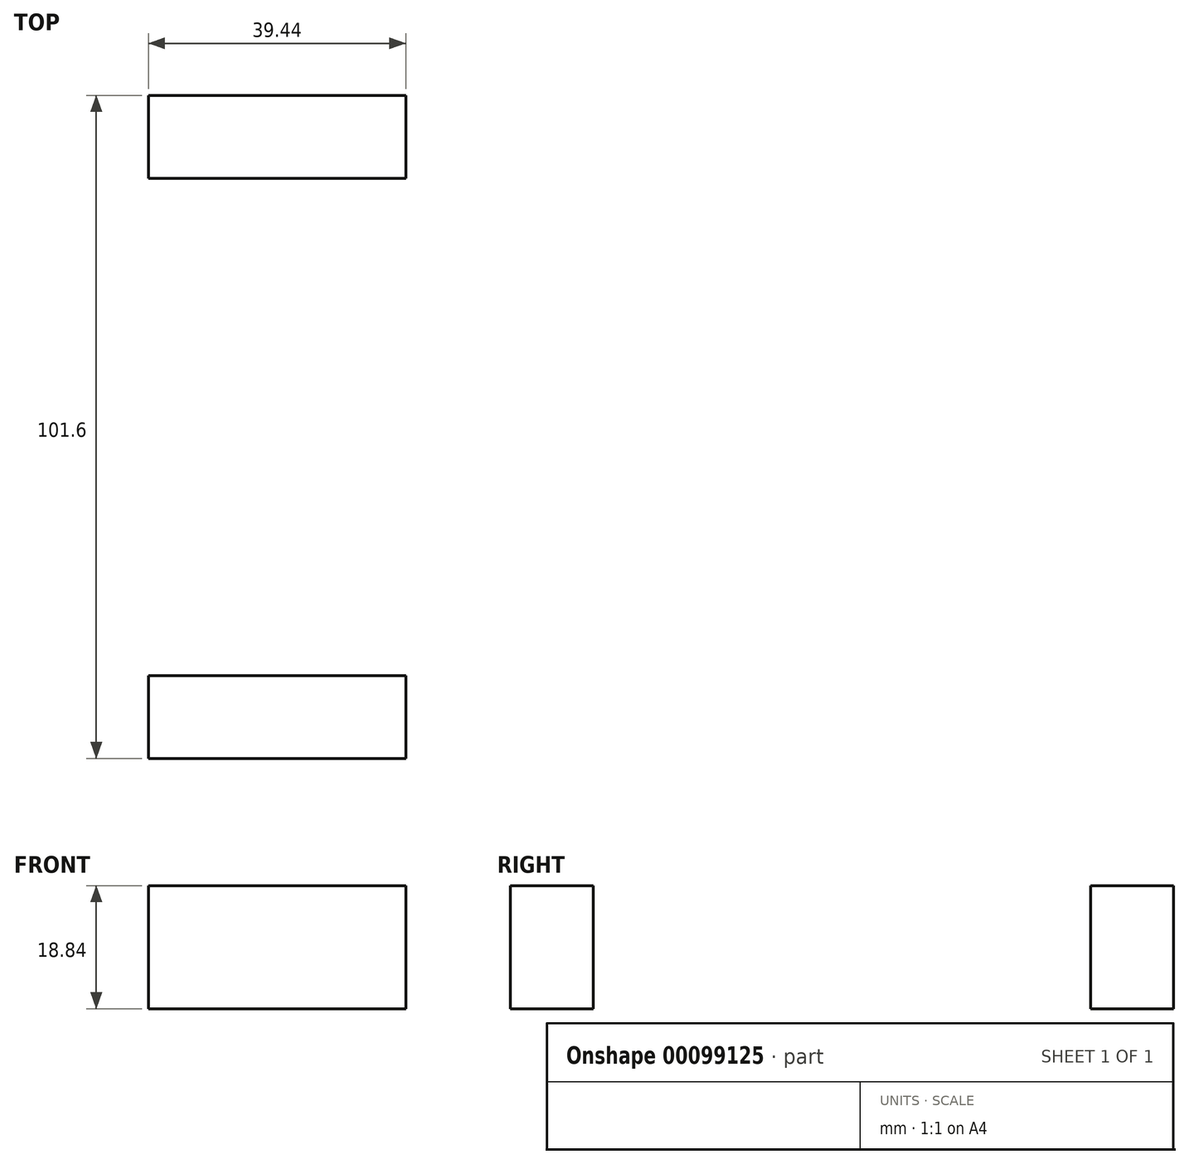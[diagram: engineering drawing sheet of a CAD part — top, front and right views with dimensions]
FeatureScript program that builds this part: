
annotation { "Feature Type Name" : "Feature", "Feature Type Description" : "" }
export const myFeature = defineFeature(function(context is Context, id is Id, definition is map)
    precondition{}
    {
        {
            var Q0;
            Q0=qCreatedBy(makeId("Front.planeOp"),FACE);
            var sketch = newSketch(context, id + "F0", { "sketchPlane" : qUnion([Q0])});
            skLineSegment(sketch, "E0.bottom", {"start": v(19.72, -9.42) * mm, "end": v(-19.72, -9.42) * mm});
            skLineSegment(sketch, "E0.top", {"start": v(19.72, 9.42) * mm, "end": v(-19.72, 9.42) * mm});
            skLineSegment(sketch, "E0.left", {"start": v(19.72, -9.42) * mm, "end": v(19.72, 9.42) * mm});
            skLineSegment(sketch, "E0.right", {"start": v(-19.72, -9.42) * mm, "end": v(-19.72, 9.42) * mm});
            skPoint(sketch, "E0.middle", {"position": v(0, 0) * mm});
            skLineSegment(sketch, "E1.bottom", {"start": v(62.56, 20.27) * mm, "end": v(34.5, 20.27) * mm});
            skLineSegment(sketch, "E1.top", {"start": v(62.56, 37.89) * mm, "end": v(34.5, 37.89) * mm});
            skLineSegment(sketch, "E1.left", {"start": v(62.56, 20.27) * mm, "end": v(62.56, 37.89) * mm});
            skLineSegment(sketch, "E1.right", {"start": v(34.5, 20.27) * mm, "end": v(34.5, 37.89) * mm});
            skPoint(sketch, "E1.middle", {"position": v(48.53, 29.08) * mm});
            skLineSegment(sketch, "E2", {"start": v(19.72, 9.42) * mm, "end": v(19.72, 16.44) * mm});
            skArc(sketch, "E3", {"start": v(19.72, 16.44) * mm, "mid": v(21.34, 20.37) * mm, "end": v(25.27, 22) * mm});
            skLineSegment(sketch, "E4", {"start": v(25.27, 22) * mm, "end": v(47.52, 22) * mm});
            skLineSegment(sketch, "E5.0", {"start": v(25.27, 33.09) * mm, "end": v(47.52, 33.09) * mm});
            skArc(sketch, "E5.1", {"start": v(8.62, 16.44) * mm, "mid": v(13.5, 28.21) * mm, "end": v(25.27, 33.09) * mm});
            skLineSegment(sketch, "E5.2", {"start": v(8.62, 9.1) * mm, "end": v(8.62, 16.44) * mm});
            skFitSpline(sketch, "E6", {"points": [v(-19.72, 9.42) * mm, v(25.27, 33.09) * mm], "startDerivative": vector(-0.22, 63.1) * mm, "endDerivative": vector(75.8, 0) * mm});
            skSolve(sketch);
        }
        {
            var Q0;
            Q0=makeQuery(id+"F0.imprint","IMPRINT",FACE,{"disambiguationData":[TD([[makeQuery(id+"F0.imprint","IMPRINT",EDGE,{"derivedFrom":sQuery(id+"F0.wireOp",EDGE,"E0.bottom")}),-1.0]])]});
            extrude(context, id + "F1", {"entities" : qUnion([Q0]), "endBound" : BoundingType.SYMMETRIC, "depth" : 101.6 * mm});
        }
        {
            var Q0;
            Q0=makeQuery(id+"F0.imprint","IMPRINT",FACE,{"disambiguationData":[TD([[makeQuery(id+"F0.imprint","IMPRINT",EDGE,{"derivedFrom":sQuery(id+"F0.wireOp",EDGE,"E0.bottom")}),-1.0]])]});
            var Q1;
            {var subQ5=sQuery(id+"F0.wireOp",EDGE,"E2");Q1=makeQuery(id+"F0.imprint","IMPRINT",FACE,{"disambiguationData":[TD([[makeQuery(id+"F0.imprint","IMPRINT",EDGE,{"derivedFrom":subQ5}),1.0]])]});}
            extrude(context, id + "F2", {"entities" : qUnion([Q0, Q1]), "operationType" : NewBodyOperationType.REMOVE, "endBound" : BoundingType.SYMMETRIC, "depth" : 76.2 * mm});
        }
        {
            var Q0;
            {var subQ4=sQuery(id+"F0.wireOp",EDGE,"E5.1");Q0=makeQuery(id+"F0.imprint","IMPRINT",FACE,{"disambiguationData":[TD([[makeQuery(id+"F0.imprint","IMPRINT",EDGE,{"derivedFrom":subQ4}),1.0]])]});}
            extrude(context, id + "F3", {"entities" : qUnion([Q0]), "operationType" : NewBodyOperationType.REMOVE, "endBound" : BoundingType.SYMMETRIC, "depth" : 50.8 * mm});
        }
    });
